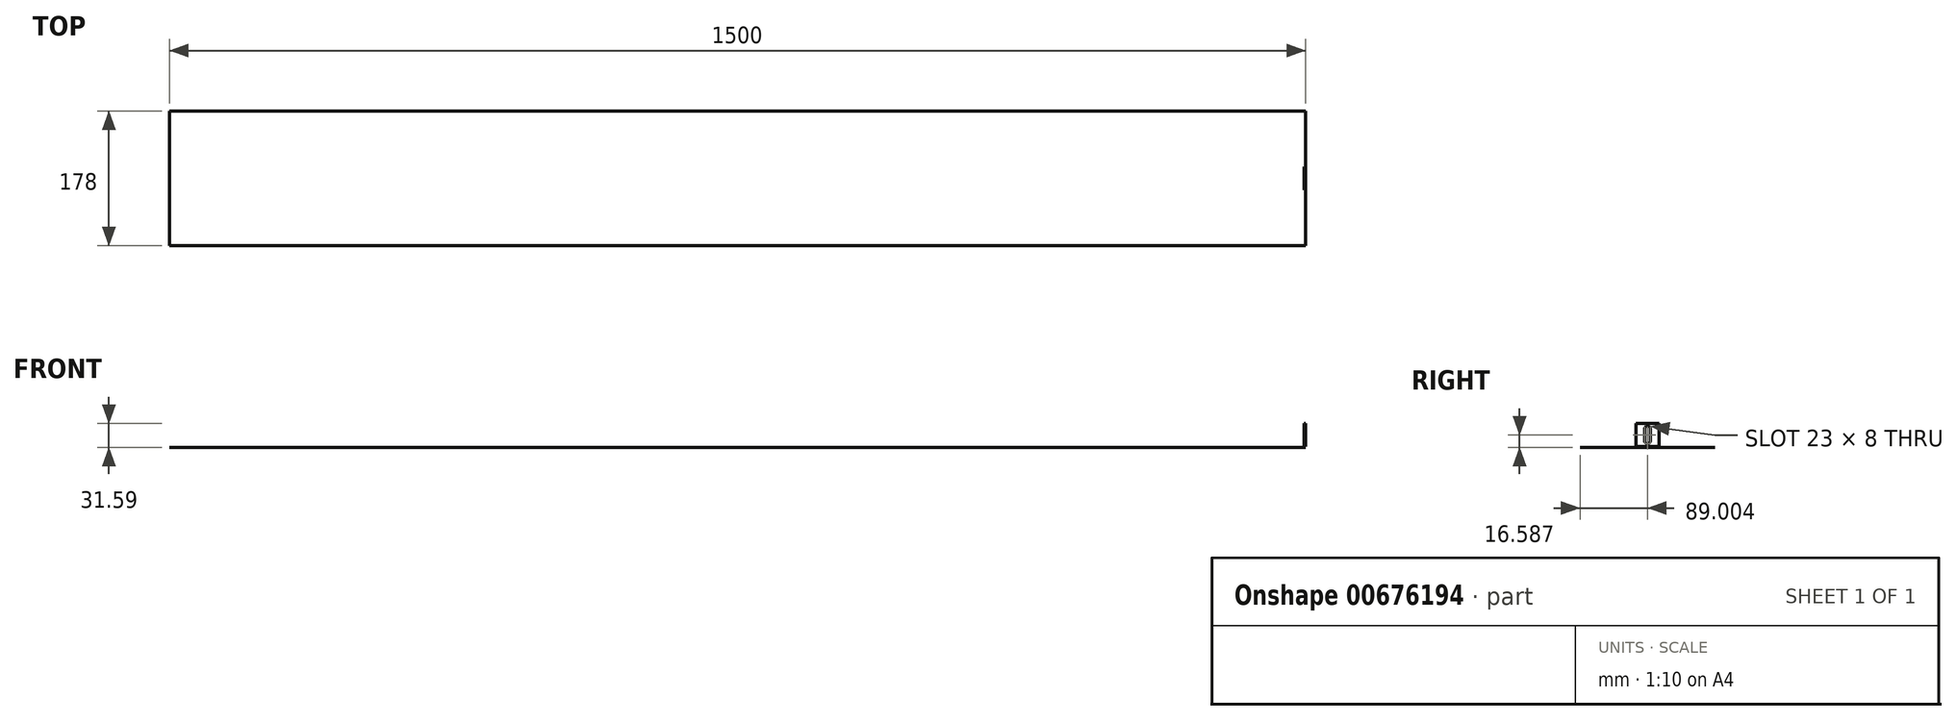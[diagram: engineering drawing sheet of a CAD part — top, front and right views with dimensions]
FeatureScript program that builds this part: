
annotation { "Feature Type Name" : "Feature", "Feature Type Description" : "" }
export const myFeature = defineFeature(function(context is Context, id is Id, definition is map)
    precondition{}
    {
        {
            var Q0;
            Q0=qCreatedBy(makeId("Top.planeOp"),FACE);
            var sketch = newSketch(context, id + "F0", { "sketchPlane" : qUnion([Q0])});
            skLineSegment(sketch, "E0.bottom", {"start": v(-76.05, 164.58) * mm, "end": v(1423.95, 164.58) * mm});
            skLineSegment(sketch, "E0.top", {"start": v(-76.05, -13.42) * mm, "end": v(1423.95, -13.42) * mm});
            skLineSegment(sketch, "E0.left", {"start": v(-76.05, 164.58) * mm, "end": v(-76.05, -13.42) * mm});
            skLineSegment(sketch, "E0.right", {"start": v(1423.95, 164.58) * mm, "end": v(1423.95, -13.42) * mm});
            skSolve(sketch);
        }
        {
            var Q0;
            Q0 = qSketchRegion(id + "F0", true);
            extrude(context, id + "F1", {"entities" : qUnion([Q0]), "depth" : 1 / 406.4 * mm, "offsetDistance" : 25.4 * mm});
        }
        {
            var Q0;
            Q0=makeQuery(id+"F1.opExtrude","SWEPT_FACE",FACE,{"disambiguationData":[OSD([sQuery(id+"F0.wireOp",EDGE,"E0.right")])]});
            var sketch = newSketch(context, id + "F2", { "sketchPlane" : qUnion([Q0])});
            skLineSegment(sketch, "E1.bottom", {"start": v(60.58, 31.59) * mm, "end": v(90.58, 31.59) * mm});
            skLineSegment(sketch, "E1.top", {"start": v(60.58, 1.59) * mm, "end": v(90.58, 1.59) * mm});
            skLineSegment(sketch, "E1.left", {"start": v(60.58, 31.59) * mm, "end": v(60.58, 1.59) * mm});
            skLineSegment(sketch, "E1.right", {"start": v(90.58, 31.59) * mm, "end": v(90.58, 1.59) * mm});
            skArc(sketch, "E2", {"start": v(79.58, 24.09) * mm, "mid": v(75.58, 28.09) * mm, "end": v(71.58, 24.09) * mm});
            skArc(sketch, "E3", {"start": v(71.58, 9.09) * mm, "mid": v(75.58, 5.09) * mm, "end": v(79.58, 9.09) * mm});
            skLineSegment(sketch, "E4", {"start": v(71.58, 24.09) * mm, "end": v(71.58, 9.09) * mm});
            skLineSegment(sketch, "E5", {"start": v(79.58, 24.09) * mm, "end": v(79.58, 9.09) * mm});
            skSolve(sketch);
        }
        {
            var Q0;
            Q0 = qSketchRegion(id + "F2", true);
            extrude(context, id + "F3", {"entities" : qUnion([Q0]), "operationType" : NewBodyOperationType.ADD, "oppositeDirection" : true, "depth" : 1.59 * mm, "offsetDistance" : 25.4 * mm});
        }
    });
